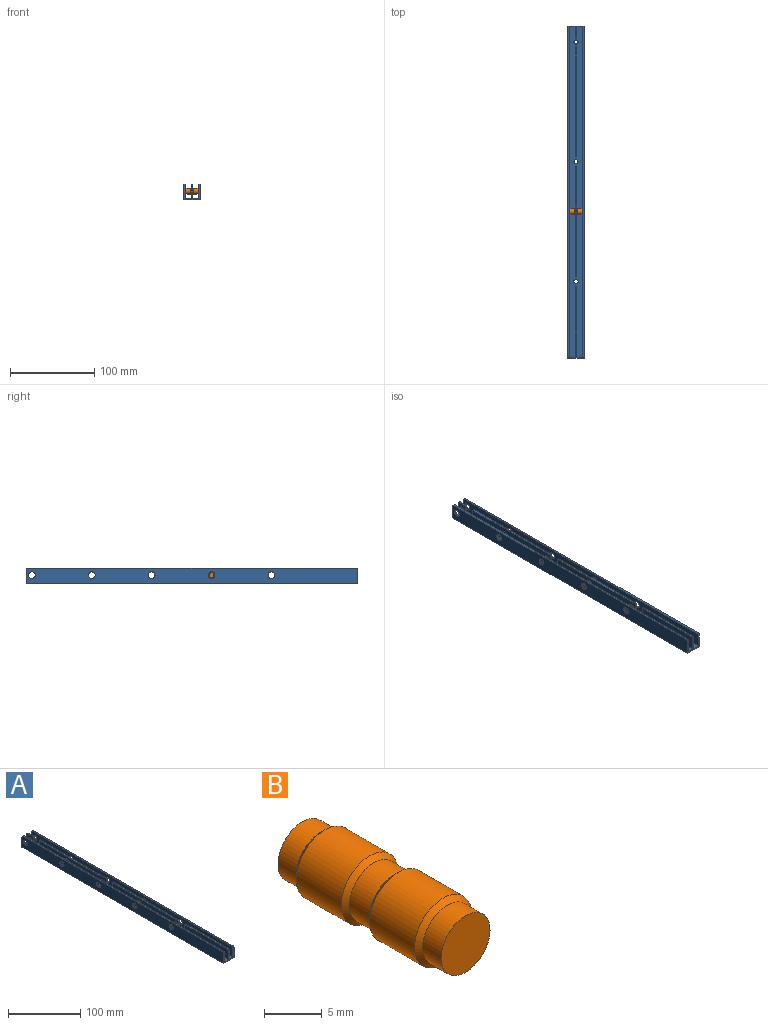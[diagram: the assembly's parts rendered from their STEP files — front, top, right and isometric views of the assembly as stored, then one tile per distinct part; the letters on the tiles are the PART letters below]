
ASSEMBLY  parts=2 mates=1
PART A: 52 faces, bbox 20x395x19 mm
  f0: plane 130.67x17mm, normal (1,0,0), area 2120.8mm2, adj f2,f6,f31,f34,f42,f43
  f1: plane 85.08x17mm, normal (1,0,0), area 1445.6mm2, adj f3,f6,f20,f45,f49
  f2: plane 130.67x2mm, normal (0,0,1), area 261.1mm2, adj f0,f5,f42,f43
  f3: plane 83.08x2mm, normal (0,0,1), area 166.1mm2, adj f1,f4,f45,f49
  f4: plane 85.08x17mm, normal (-1,0,0), area 1445.6mm2, adj f3,f6,f20,f45,f49
  f5: plane 130.67x17mm, normal (-1,0,0), area 2120.8mm2, adj f2,f6,f31,f34,f42,f43
  f6: plane 395x16mm, normal (0,0,1), area 5542.8mm2, adj f0,f1,f4,f5,f7,f9,f10,f12
  f7: plane 130.67x17mm, normal (1,0,0), area 2120.8mm2, adj f6,f8,f25,f28,f39,f40
  f8: plane 130.67x2mm, normal (0,0,1), area 261.1mm2, adj f7,f9,f39,f40
  f9: plane 130.67x17mm, normal (-1,0,0), area 2120.8mm2, adj f6,f8,f25,f28,f39,f40
  f10: plane 17x13.08mm, normal (1,0,0), area 171.3mm2, adj f6,f11,f21,f22,f37,f46
  f11: plane 11.08x2mm, normal (0,0,1), area 22.1mm2, adj f10,f12,f37,f46
  f12: plane 17x13.08mm, normal (-1,0,0), area 171.3mm2, adj f6,f11,f21,f22,f37,f46
  f13: plane 395x17mm, normal (1,0,0), area 6462mm2, adj f6,f14,f20,f21,f24,f27,f30,f33
  f14: plane 391x2mm, normal (0,0,1), area 782mm2, adj f13,f15,f48,f51
  f15: plane 395x19mm, normal (-1,0,0), area 7252mm2, adj f14,f16,f20,f21,f24,f27,f30,f33
  f16: plane 395x20mm, normal (0,0,-1), area 7841.1mm2, adj f15,f17,f20,f21,f38,f41,f44
  f17: plane 395x19mm, normal (1,0,0), area 7252mm2, adj f16,f18,f20,f21,f23,f26,f29,f32
  f18: plane 391x2mm, normal (0,0,1), area 782mm2, adj f17,f19,f47,f50
  f19: plane 395x17mm, normal (-1,0,0), area 6462mm2, adj f6,f18,f20,f21,f23,f26,f29,f32
  f20: plane 20x17mm, normal (0,-1,0), area 130mm2, adj f1,f4,f6,f13,f15,f16,f17,f19
  f21: plane 20x17mm, normal (0,1,0), area 130mm2, adj f6,f10,f12,f13,f15,f16,f17,f19
  f22: cylinder r=4mm len=8mm, axis (1,0,0), area 50.3mm2, adj f10,f12
  f23: cylinder r=4mm len=8mm, axis (1,0,0), area 50.3mm2, adj f17,f19
  f24: cylinder r=4mm len=8mm, axis (1,0,0), area 50.3mm2, adj f13,f15
  f25: cylinder r=4mm len=8mm, axis (1,0,0), area 50.3mm2, adj f7,f9
  f26: cylinder r=4mm len=8mm, axis (1,0,0), area 50.3mm2, adj f17,f19
  f27: cylinder r=4mm len=8mm, axis (1,0,0), area 50.3mm2, adj f13,f15
  f28: cylinder r=4mm len=8mm, axis (1,0,0), area 50.3mm2, adj f7,f9
  f29: cylinder r=4mm len=8mm, axis (1,0,0), area 50.3mm2, adj f17,f19
  f30: cylinder r=4mm len=8mm, axis (1,0,0), area 50.3mm2, adj f13,f15
  f31: cylinder r=4mm len=8mm, axis (1,0,0), area 50.3mm2, adj f0,f5
  f32: cylinder r=4mm len=8mm, axis (1,0,0), area 50.3mm2, adj f17,f19
  f33: cylinder r=4mm len=8mm, axis (1,0,0), area 50.3mm2, adj f13,f15
  f34: cylinder r=4mm len=8mm, axis (1,0,0), area 50.3mm2, adj f0,f5
  f35: cylinder r=4mm len=8mm, axis (1,0,0), area 50.3mm2, adj f17,f19
  f36: cylinder r=4mm len=8mm, axis (1,0,0), area 50.3mm2, adj f13,f15
  f37: cylinder r=6mm len=17mm, axis (0,0,1), area 34.2mm2, adj f6,f10,f11,f12
  f38: cylinder r=2.5mm len=5mm, axis (0,0,1), area 31.4mm2, adj f6,f16
  f39: cylinder r=6mm len=17mm, axis (0,0,1), area 34.2mm2, adj f6,f7,f8,f9
  f40: cylinder r=6mm len=17mm, axis (0,0,1), area 34.2mm2, adj f6,f7,f8,f9
  f41: cylinder r=2.5mm len=5mm, axis (0,0,1), area 31.4mm2, adj f6,f16
  f42: cylinder r=6mm len=17mm, axis (0,0,1), area 34.2mm2, adj f0,f2,f5,f6
  f43: cylinder r=6mm len=17mm, axis (0,0,1), area 34.2mm2, adj f0,f2,f5,f6
  f44: cylinder r=2.5mm len=5mm, axis (0,0,1), area 31.4mm2, adj f6,f16
  f45: cylinder r=6mm len=17mm, axis (0,0,1), area 34.2mm2, adj f1,f3,f4,f6
  f46: cylinder r=2mm len=2mm, axis (-1,0,0), area 6.3mm2, adj f10,f11,f12,f21
  f47: cylinder r=2mm len=2mm, axis (-1,0,0), area 6.3mm2, adj f17,f18,f19,f21
  f48: cylinder r=2mm len=2mm, axis (-1,0,0), area 6.3mm2, adj f13,f14,f15,f21
  f49: cylinder r=2mm len=2mm, axis (1,0,0), area 6.3mm2, adj f1,f3,f4,f20
  f50: cylinder r=2mm len=2mm, axis (1,0,0), area 6.3mm2, adj f17,f18,f19,f20
  f51: cylinder r=2mm len=2mm, axis (1,0,0), area 6.3mm2, adj f13,f14,f15,f20
PART B: 11 faces, bbox 7x20x7 mm
  f0: plane 6x6mm, normal (0,-1,0), area 28.3mm2, adj f6
  f1: plane 6x6mm, normal (0,1,0), area 28.3mm2, adj f2
  f2: cylinder r=3mm len=6mm, axis (0,1,0), area 42.4mm2, adj f1,f7
  f3: cylinder r=3.5mm len=7mm, axis (0,1,0), area 121mm2, adj f7,f8
  f4: cylinder r=3mm len=6mm, axis (0,1,0), area 47.1mm2, adj f8,f9
  f5: cylinder r=3.5mm len=7mm, axis (0,1,0), area 121mm2, adj f9,f10
  f6: cylinder r=3mm len=6mm, axis (0,1,0), area 42.4mm2, adj f0,f10
  f7: cone r=3mm half-angle=45deg, axis (0,-1,0), area 14.4mm2, adj f2,f3
  f8: cone r=3.5mm half-angle=45deg, axis (0,1,0), area 14.4mm2, adj f3,f4
  f9: cone r=3mm half-angle=45deg, axis (0,-1,0), area 14.4mm2, adj f4,f5
  f10: cone r=3.5mm half-angle=45deg, axis (0,1,0), area 14.4mm2, adj f5,f6
PLACE A t=(-59.94,107.32,-73.57)mm
PLACE B rot(axis=(-0.58,0.58,0.58),120deg) t=(-157.23,-113.43,-72.95)mm
MATE fastened A.f31 <-> B.f2  axis (1,0,0) through (-57.94,-113.43,-72.95)mm
